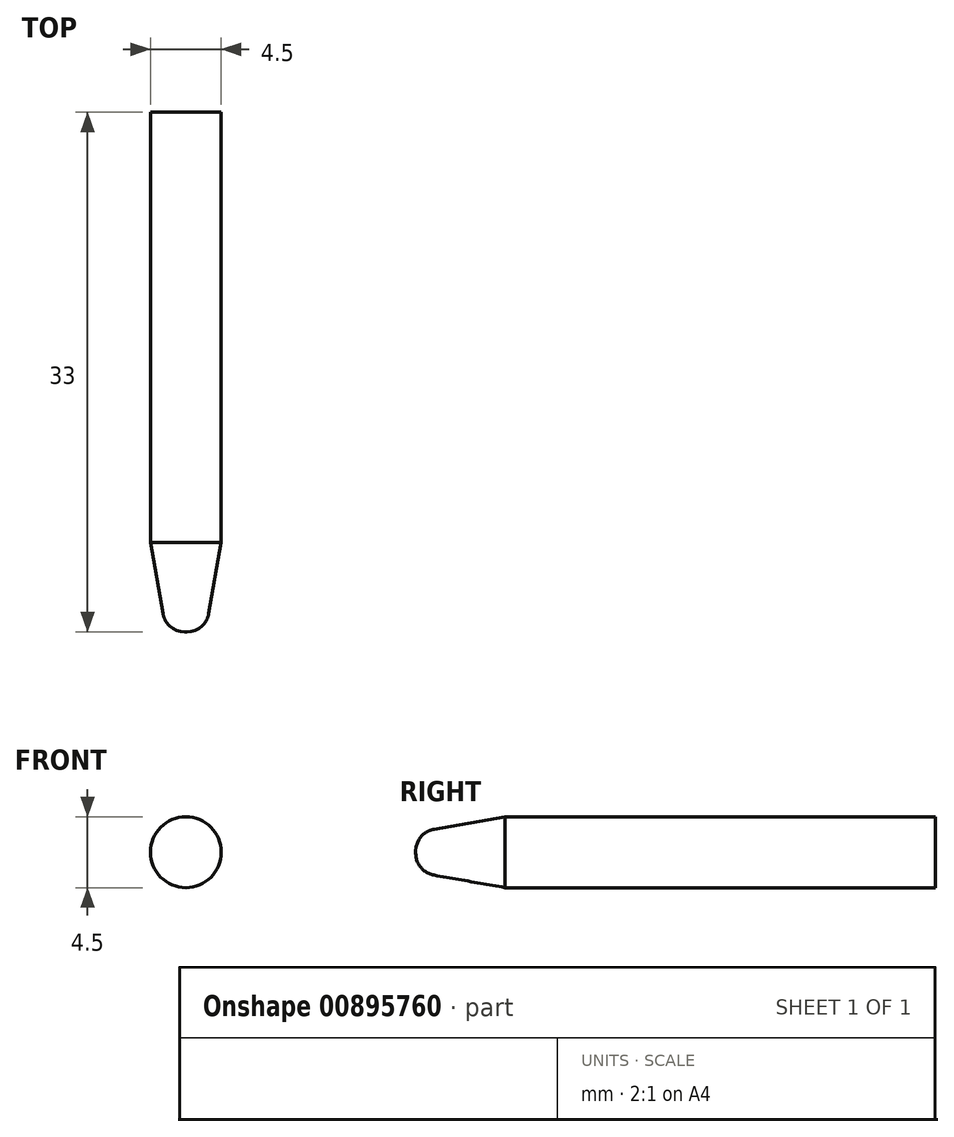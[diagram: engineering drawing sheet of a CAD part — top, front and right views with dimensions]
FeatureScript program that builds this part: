
annotation { "Feature Type Name" : "Feature", "Feature Type Description" : "" }
export const myFeature = defineFeature(function(context is Context, id is Id, definition is map)
    precondition{}
    {
        {
            var Q0;
            Q0=qCreatedBy(makeId("Front.planeOp"),FACE);
            var sketch = newSketch(context, id + "F0", { "sketchPlane" : qUnion([Q0])});
            skCircle(sketch, "E0", {"center": v(0, 0) * mm, "radius": 2.25 * mm});
            skSolve(sketch);
        }
        {
            var Q0;
            Q0=makeQuery(id+"F0.imprint","IMPRINT",FACE,{"disambiguationData":[TD([[makeQuery(id+"F0.imprint","IMPRINT",EDGE,{"derivedFrom":sQuery(id+"F0.wireOp",EDGE,"E0")}),1.0]])]});
            var Q1;
            Q1=sQuery(id+"F0.wireOp",EDGE,"E0");
            extrude(context, id + "F1", {"entities" : qUnion([Q0]), "surfaceEntities" : qUnion([Q1]), "offsetDistance" : 25 * mm, "depth" : 33 * mm});
        }
        {
            var Q0;
            Q0=makeQuery(id+"F1.opExtrude","CAP_FACE",FACE,{"disambiguationData":[OSD([sQuery(id+"F0.wireOp",EDGE,"E0")])],"isStart":false});
            chamfer(context, id + "F2", {"entities" : qUnion([Q0]), "chamferType" : ChamferType.OFFSET_ANGLE, "width" : 1 * mm, "oppositeDirection" : false, "angle" : 80 * degree, "tangentPropagation" : true});
        }
        {
            var Q0;
            Q0=makeQuery(id+"F1.opExtrude","CAP_FACE",FACE,{"disambiguationData":[OSD([sQuery(id+"F0.wireOp",EDGE,"E0")])],"isStart":false});
            fillet(context, id + "F3", {"entities" : qUnion([Q0]), "radius" : 1.4 * mm, "tangentPropagation" : true, "allowEdgeOverflow" : false});
        }
    });
